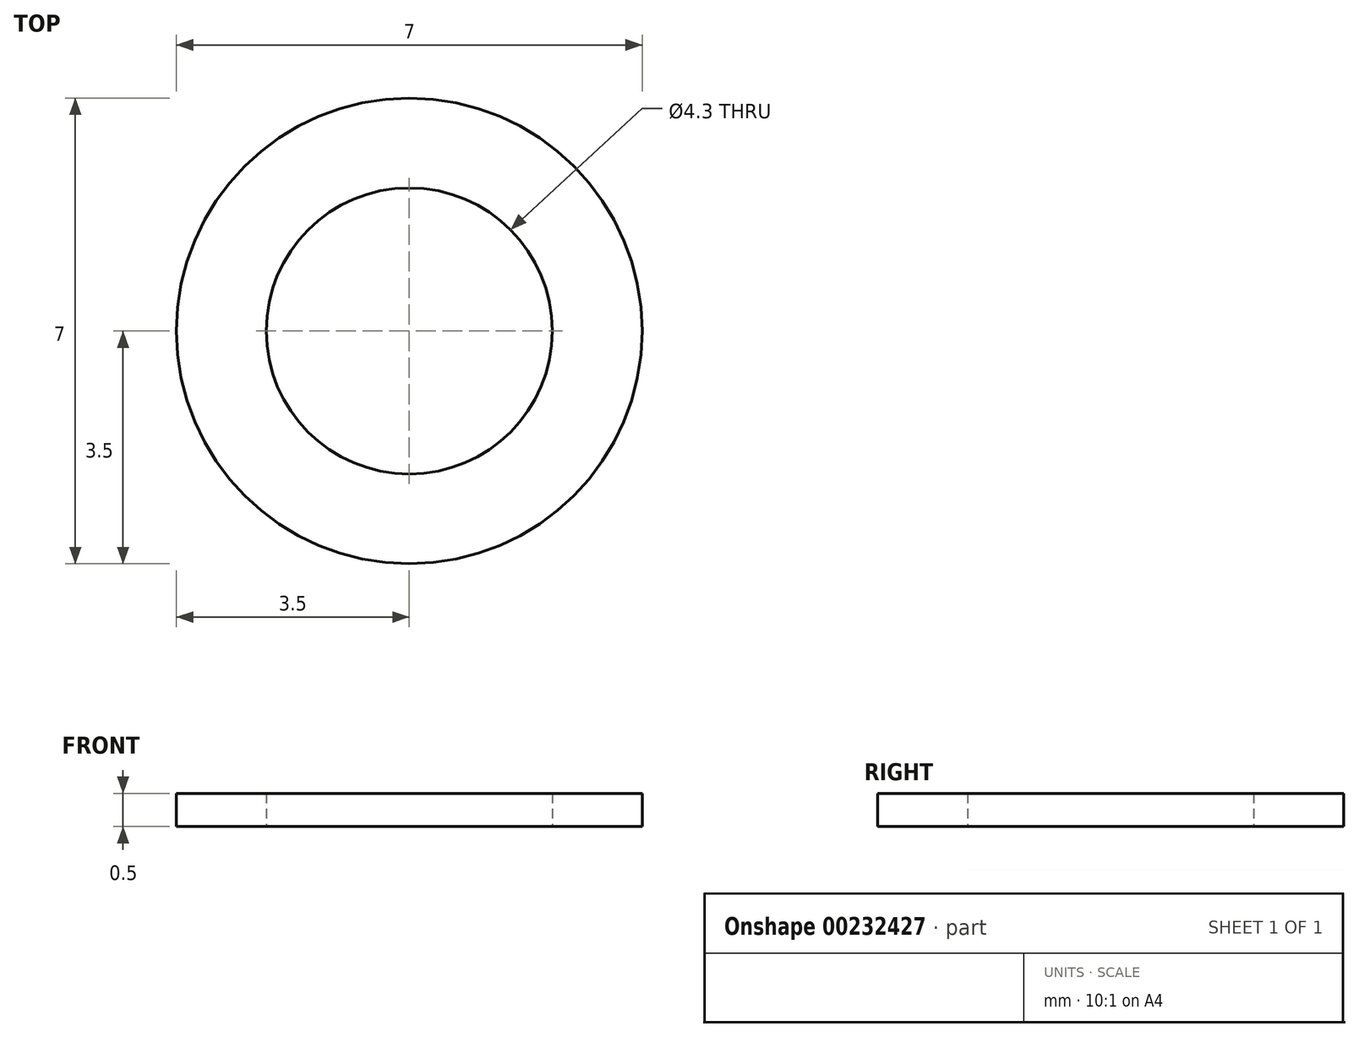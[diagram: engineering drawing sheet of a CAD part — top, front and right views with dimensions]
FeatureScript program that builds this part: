
annotation { "Feature Type Name" : "Feature", "Feature Type Description" : "" }
export const myFeature = defineFeature(function(context is Context, id is Id, definition is map)
    precondition{}
    {
        {
            var Q0;
            Q0=qCreatedBy(makeId("Top.planeOp"),FACE);
            var sketch = newSketch(context, id + "F0", { "sketchPlane" : qUnion([Q0])});
            skCircle(sketch, "E0", {"center": v(0, 0) * mm, "radius": 3.5 * mm});
            skCircle(sketch, "E1", {"center": v(0, 0) * mm, "radius": 2.15 * mm});
            skSolve(sketch);
        }
        {
            var Q0;
            Q0=makeQuery(id+"F0.imprint","IMPRINT",FACE,{"disambiguationData":[TD([[makeQuery(id+"F0.imprint","IMPRINT",EDGE,{"derivedFrom":sQuery(id+"F0.wireOp",EDGE,"E0")}),1.0]])]});
            extrude(context, id + "F1", {"entities" : qUnion([Q0]), "endBound" : BoundingType.SYMMETRIC, "depth" : 0.5 * mm});
        }
    });
